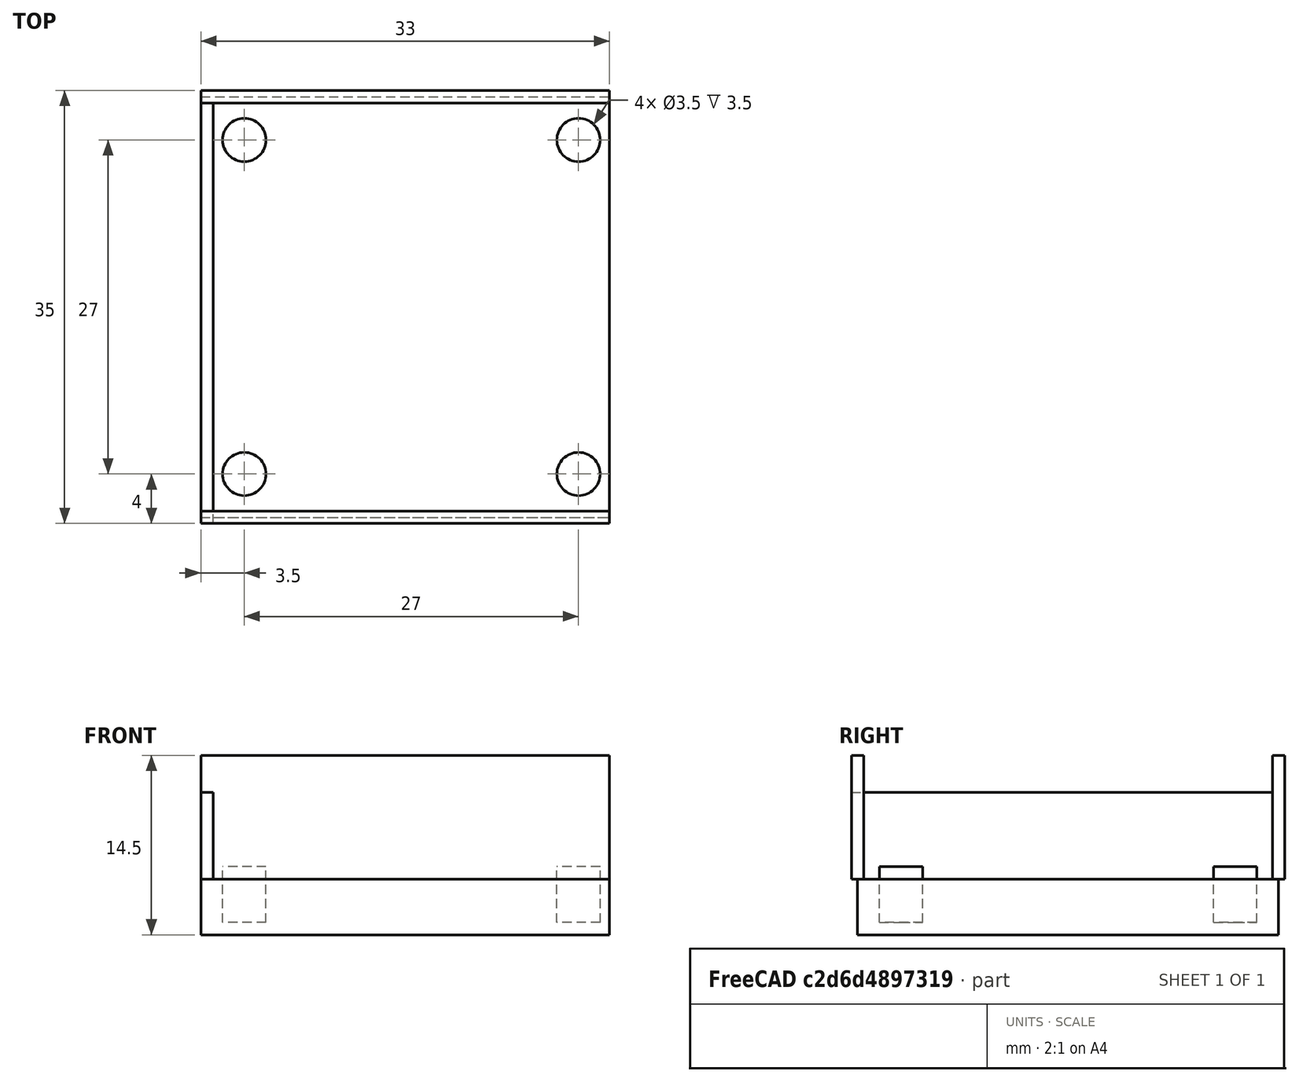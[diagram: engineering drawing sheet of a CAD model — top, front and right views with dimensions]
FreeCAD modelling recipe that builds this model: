
FCSTD DOCUMENT  (FreeCAD 0.17R13519 (Git))
Label: Case
License: All rights reserved
LicenseURL: http://en.wikipedia.org/wiki/All_rights_reserved
objects: PartDesign::Body×9, PartDesign::AdditiveBox×5, PartDesign::AdditiveCylinder×4, PartDesign::Boolean×2, Sketcher::SketchObject×1
note: 30 computed .brp shape members not serialized (recipe doc carries the construction recipe); baked Part::Feature solids carry a one-line shape summary decoded from their .brp

FEATURE [PartDesign::AdditiveBox] Box
  AttacherType = Attacher::AttachEngine3D
  Height = 4.5
  Length = 33
  MapMode = 1
  Width = 34
FEATURE [Sketcher::SketchObject] Sketch
  MapMode = 5
  Support = -> [XY_Plane]
FEATURE [PartDesign::AdditiveCylinder] Cylinder
  Angle = 360
  AttacherType = Attacher::AttachEngine3D
  AttachmentOffset = pos=(3.5,3.5,-3.5) rot=(0,0,1;0rad)
  Height = 4.5
  MapMode = 5
  Placement = pos=(3.5,3.5,1) rot=(0,0,1;0rad)
  Radius = 1.75
  Support = -> [Box]
FEATURE [PartDesign::Body] Body001  label="hole3"
  Group = -> [Cylinder]
  Origin = -> Origin001
  Tip = -> Cylinder
FEATURE [PartDesign::AdditiveCylinder] Cylinder001
  Angle = 360
  AttacherType = Attacher::AttachEngine3D
  AttachmentOffset = pos=(3.5,30.5,-3.5) rot=(0,0,1;0rad)
  Height = 4.5
  MapMode = 5
  Placement = pos=(3.5,30.5,1) rot=(0,0,1;0rad)
  Radius = 1.75
  Support = -> [Box]
FEATURE [PartDesign::Body] Body002  label="hole1"
  Group = -> [Cylinder001]
  Origin = -> Origin002
  Tip = -> Cylinder001
FEATURE [PartDesign::AdditiveCylinder] Cylinder002
  Angle = 360
  AttacherType = Attacher::AttachEngine3D
  AttachmentOffset = pos=(30.5,3.5,-3.5) rot=(0,0,1;0rad)
  Height = 4.5
  MapMode = 5
  Placement = pos=(30.5,3.5,1) rot=(0,0,1;0rad)
  Radius = 1.75
  Support = -> [Box]
FEATURE [PartDesign::Body] Body003  label="hole4"
  Group = -> [Cylinder002]
  Origin = -> Origin003
  Tip = -> Cylinder002
FEATURE [PartDesign::AdditiveCylinder] Cylinder003
  Angle = 360
  AttacherType = Attacher::AttachEngine3D
  AttachmentOffset = pos=(30.5,30.5,-3.5) rot=(0,0,1;0rad)
  Height = 4.5
  MapMode = 5
  Placement = pos=(30.5,30.5,1) rot=(0,0,1;0rad)
  Radius = 1.75
  Support = -> [Box]
FEATURE [PartDesign::Body] Body004  label="hole2"
  Group = -> [Cylinder003]
  Origin = -> Origin004
  Tip = -> Cylinder003
FEATURE [PartDesign::AdditiveBox] Box001
  AttacherType = Attacher::AttachEngine3D
  AttachmentOffset = pos=(0,-0.5,0) rot=(0,0,1;0rad)
  Height = 7
  Length = 1
  MapMode = 5
  Placement = pos=(0,-0.5,4.5) rot=(0,0,1;0rad)
  Support = -> [Box]
  Width = 34
FEATURE [PartDesign::Body] Body005
  Group = -> [Box001]
  Origin = -> Origin005
  Tip = -> Box001
FEATURE [PartDesign::AdditiveBox] Box002
  AttacherType = Attacher::AttachEngine3D
  AttachmentOffset = pos=(0,-0.5,0) rot=(0,0,1;0rad)
  Height = 10
  Length = 33
  MapMode = 5
  Placement = pos=(0,-0.5,4.5) rot=(0,0,1;0rad)
  Support = -> [Box]
  Width = 1
FEATURE [PartDesign::Body] Body006
  Group = -> [Box002]
  Origin = -> Origin006
  Tip = -> Box002
FEATURE [PartDesign::AdditiveBox] Box003
  AttacherType = Attacher::AttachEngine3D
  AttachmentOffset = pos=(0,33.5,0) rot=(0,0,1;0rad)
  Height = 10
  Length = 33
  MapMode = 5
  Placement = pos=(0,33.5,4.5) rot=(0,0,1;0rad)
  Support = -> [Box]
  Width = 1
FEATURE [PartDesign::Body] Body007
  Group = -> [Box003]
  Origin = -> Origin007
  Tip = -> Box003
FEATURE [PartDesign::AdditiveBox] Box004
  AttacherType = Attacher::AttachEngine3D
  AttachmentOffset = pos=(0,-0.5,0) rot=(0,0,1;0rad)
  Height = 10
  Length = 33
  MapMode = 5
  Placement = pos=(0,-0.5,4.5) rot=(0,0,1;0rad)
  Support = -> [Box]
  Width = 1
FEATURE [PartDesign::Body] Body008
  Group = -> [Box004]
  Origin = -> Origin008
  Tip = -> Box004
FEATURE [PartDesign::Boolean] Boolean
  BaseFeature = -> Box
  Group = -> [Body006,Body005,Body007,Body008]
  Type = 0
FEATURE [PartDesign::Boolean] Boolean001
  BaseFeature = -> Boolean
  Group = -> [Body001,Body002,Body004,Body003]
  Type = 1
FEATURE [PartDesign::Body] Body  label="base"
  Group = -> [Box,Sketch,Boolean,Boolean001]
  Origin = -> Origin
  Tip = -> Boolean001
